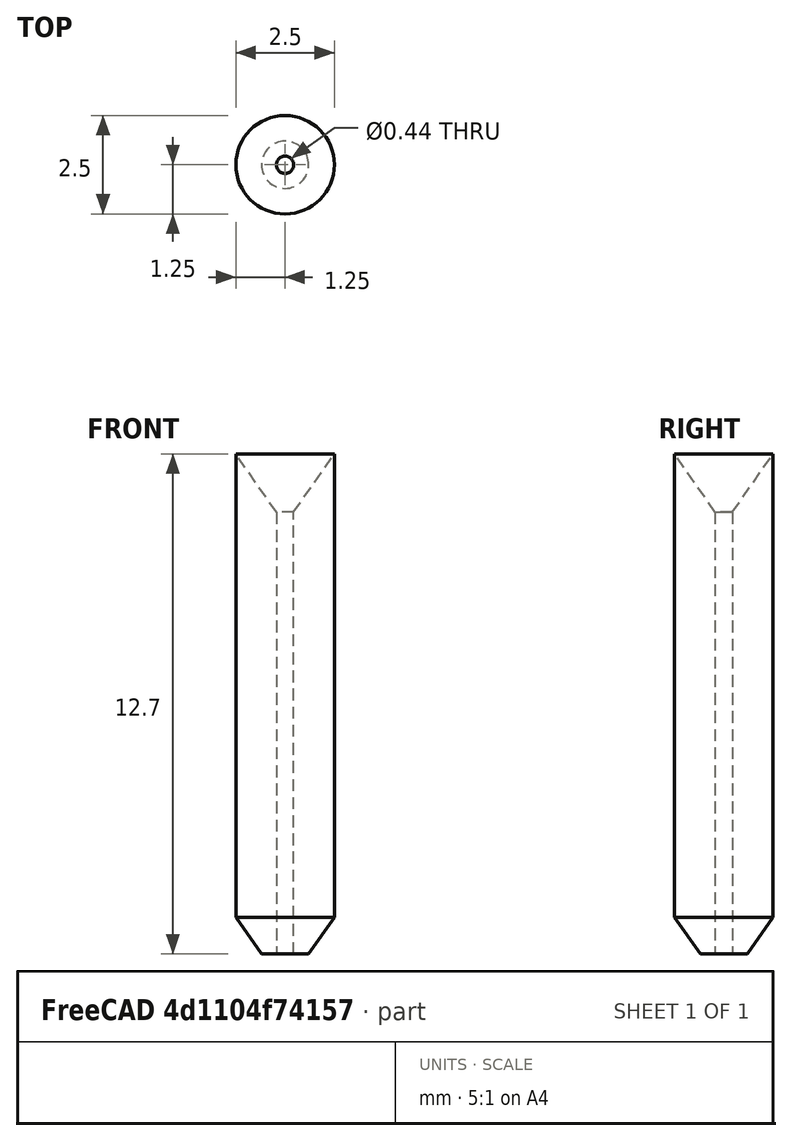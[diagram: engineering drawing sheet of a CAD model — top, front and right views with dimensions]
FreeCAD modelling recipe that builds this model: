
FCSTD DOCUMENT  (FreeCAD 0.21R0.21.2)
Label: FiberFerruleParameterized
License: All rights reserved
LicenseURL: https://en.wikipedia.org/wiki/All_rights_reserved
objects: Part::Cylinder×2, Part::Cone×2, Part::MultiFuse×2, Spreadsheet::Sheet×1, Part::Cut×1
note: 7 computed .brp shape members not serialized (recipe doc carries the construction recipe); baked Part::Feature solids carry a one-line shape summary decoded from their .brp

FEATURE [Spreadsheet::Sheet] Spreadsheet  label="FerruleConfig"
  cells = A2='Ferrule OD; B2(ferrule_od)=2.5; C2='outer diameter; D2='typ. 2.5mm or 1.25mm; A3='Ferrule ID; B3(ferrule_id)=0.44; C3='Inner diameter; D3='typ. 440 um / 125um / 231 um; A4='Ferrule Length; B4(ferrule_length)=12.7; C4='Ferrule length; D4='typ 12.7mm / 10.5mm; A5='Front angle; B5(ferrule_front_angle)=35; C5='Angle on front; D5='typ 35 deg; A6='Back angle; B6(ferrule_back_angle)=35; C6='Angle on back; D6='typ 35 deg
FEATURE [Part::Cylinder] Cylinder
  Angle = 360
  AttacherType = Attacher::AttachEngine3D
  FirstAngle = 0
  Height = 11.7717
  Placement = pos=(0,0,0.928296) rot=(0,0,1;0rad)
  Radius = 1.25
  SecondAngle = 0
  expr: .Placement.Base.z = (<<FerruleConfig>>.ferrule_od - 1.2) / (2 * tan(<<FerruleConfig>>.ferrule_front_angle))
  expr: Height = <<FerruleConfig>>.ferrule_length - (<<FerruleConfig>>.ferrule_od - 1.2) / (2 * tan(<<FerruleConfig>>.ferrule_front_angle))
  expr: Radius = <<FerruleConfig>>.ferrule_od / 2
FEATURE [Part::Cylinder] Cylinder001
  Angle = 360
  AttacherType = Attacher::AttachEngine3D
  FirstAngle = 0
  Height = 12.7
  Radius = 0.22
  SecondAngle = 0
  expr: Height = <<FerruleConfig>>.ferrule_length
  expr: Radius = <<FerruleConfig>>.ferrule_id / 2
FEATURE [Part::Cone] Cone
  Angle = 360
  AttacherType = Attacher::AttachEngine3D
  Height = 0.928296
  Radius1 = 0.6
  Radius2 = 1.25
  expr: Height = (<<FerruleConfig>>.ferrule_od - 1.2) / (2 * tan(<<FerruleConfig>>.ferrule_front_angle))
  expr: Radius2 = <<FerruleConfig>>.ferrule_od / 2
FEATURE [Part::MultiFuse] Fusion
  Shapes = -> [Cylinder,Cone]
FEATURE [Part::Cone] Cone001
  Angle = 360
  AttacherType = Attacher::AttachEngine3D
  Height = 1.47099
  Placement = pos=(0,0,11.229) rot=(0,0,1;0rad)
  Radius1 = 0.22
  Radius2 = 1.25
  expr: .Placement.Base.z = <<FerruleConfig>>.ferrule_length - (<<FerruleConfig>>.ferrule_od - <<FerruleConfig>>.ferrule_id) / (2 * tan(<<FerruleConfig>>.ferrule_back_angle))
  expr: Height = (<<FerruleConfig>>.ferrule_od - <<FerruleConfig>>.ferrule_id) / (2 * tan(<<FerruleConfig>>.ferrule_back_angle))
  expr: Radius1 = <<FerruleConfig>>.ferrule_id / 2
  expr: Radius2 = <<FerruleConfig>>.ferrule_od / 2
FEATURE [Part::MultiFuse] Fusion001
  Shapes = -> [Cylinder001,Cone001]
FEATURE [Part::Cut] Cut  label="FiberFerrule"
  Base = -> Fusion
  Tool = -> Fusion001
